# Revit family: Towel_Bar-DXV-Rem-D35100240_Series
name_source: partatom
category: Specialty Equipment
units: mm (PartAtom-declared; Revit-internal decimal feet)

## family parameters
Cut with Voids When Loaded = No
Host = Face
OmniClass Number = 23.40.20.21.27
OmniClass Title = Towel Bars
Part Type = Normal
Room Calculation Point = No
Round Connector Dimension = Use Diameter
Shared = Yes

## types (2) — shared parameters
Assembly Code = C1030200
Default Elevation = 48"
Description = 24" Towel Bar
Height = 2"
Installation Type = Surface Mounted
Length = 3"
Manufacturer = DXV
Price = Prices may vary. Please consult Manufacturer Representative for most up-to-date price list.
Product Documentation Link = http://dxv01.blob.core.windows.net
Product Page URL = http://www.dxv.com
Revised Date = 11/11/21
URL = http://www.dxv.com
Warranty Documentation Link = https://www.dxv.com
Width = 24 3/8"

## per-type parameters (varying)
| type | Finish | Material |
| D35100240.100 | Brass-DXV-100-Polished Chrome | Brass-DXV-100-Polished Chrome |
| D35100240.144 | Brass-DXV-144-Brushed Nickel | Brass-DXV-144-Brushed Nickel |

note: column(s) folded — value = type name in every type: Model

## geometry (parser evidence)
native form markers: Sweep x3
no freeform markers — native parametric forms only
